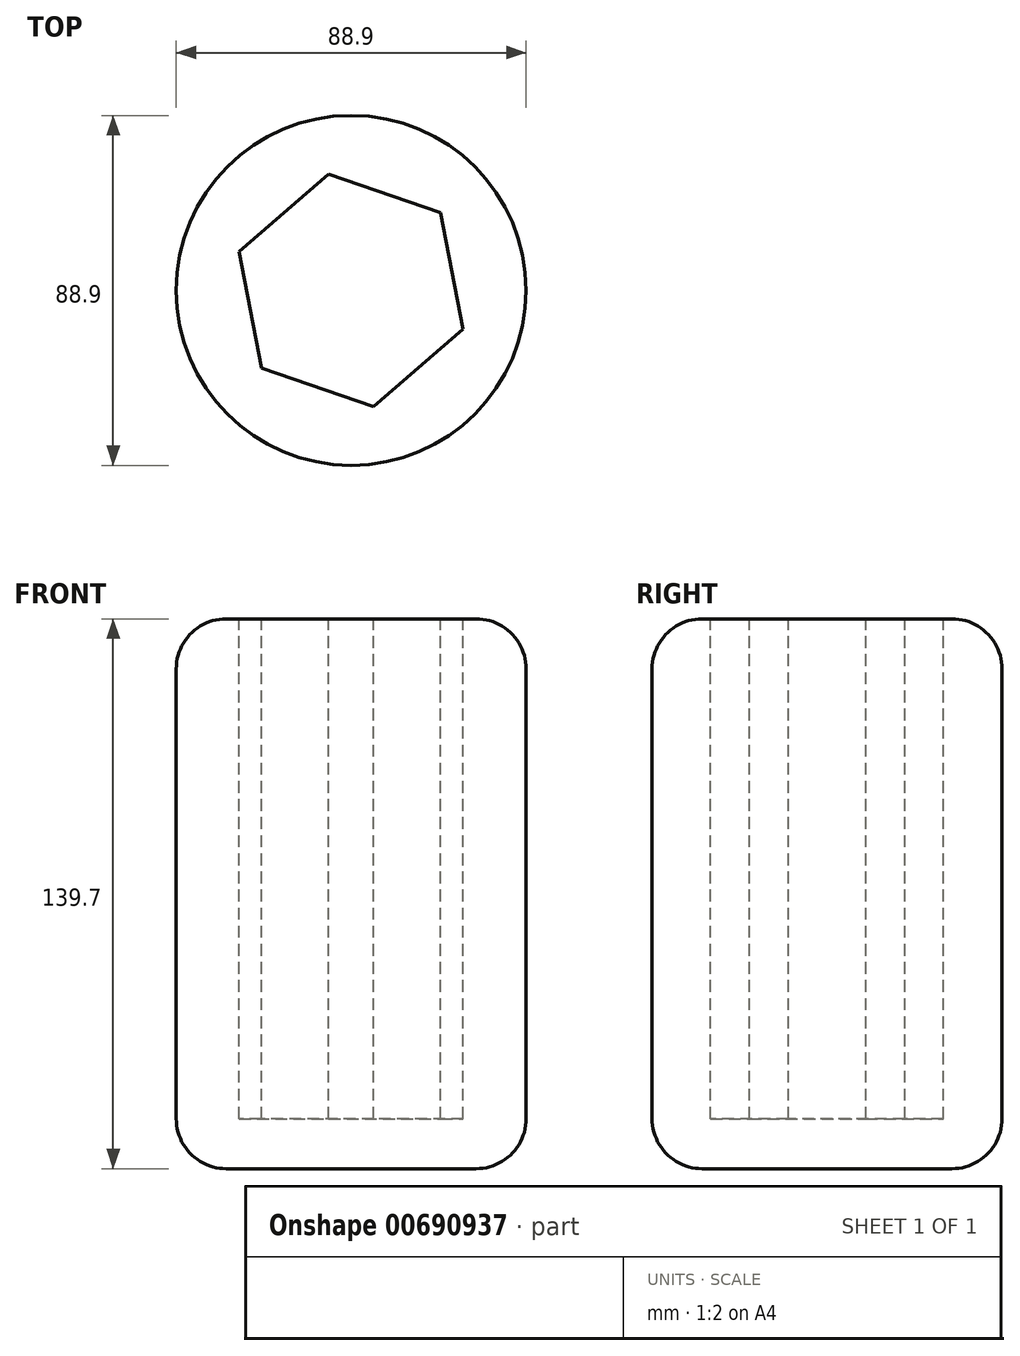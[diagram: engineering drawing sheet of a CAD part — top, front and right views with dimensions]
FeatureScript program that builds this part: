
annotation { "Feature Type Name" : "Feature", "Feature Type Description" : "" }
export const myFeature = defineFeature(function(context is Context, id is Id, definition is map)
    precondition{}
    {
        {
            var Q0;
            Q0=qCreatedBy(makeId("Top.planeOp"),FACE);
            var sketch = newSketch(context, id + "F0", { "sketchPlane" : qUnion([Q0])});
            skCircle(sketch, "E0", {"center": v(0, 0) * mm, "radius": 44.45 * mm});
            skSolve(sketch);
        }
        {
            var Q0;
            Q0 = qSketchRegion(id + "F0", true);
            extrude(context, id + "F1", {"entities" : qUnion([Q0]), "depth" : 139.7 * mm, "offsetDistance" : 25.4 * mm});
        }
        {
            var Q0;
            Q0=makeQuery(id+"F1.opExtrude","CAP_EDGE",EDGE,{"disambiguationData":[OSD([sQuery(id+"F0.wireOp",EDGE,"E0")])],"isStart":true});
            var Q1;
            Q1=makeQuery(id+"F1.opExtrude","CAP_EDGE",EDGE,{"disambiguationData":[OSD([sQuery(id+"F0.wireOp",EDGE,"E0")])],"isStart":false});
            fillet(context, id + "F2", {"entities" : qUnion([Q0, Q1]), "radius" : 12.7 * mm, "tangentPropagation" : true, "allowEdgeOverflow" : false});
        }
        {
            var Q0;
            Q0=makeQuery(id+"F1.opExtrude","CAP_FACE",FACE,{"disambiguationData":[OSD([sQuery(id+"F0.wireOp",EDGE,"E0")])],"isStart":false});
            var sketch = newSketch(context, id + "F3", { "sketchPlane" : qUnion([Q0])});
            skCircle(sketch, "E1", {"center": v(0, 0) * mm, "radius": 22.92 * mm});
            skSolve(sketch);
        }
        {
            var Q0;
            Q0 = qSketchRegion(id + "F3", true);
            extrude(context, id + "F4", {"entities" : qUnion([Q0]), "operationType" : NewBodyOperationType.REMOVE, "oppositeDirection" : true, "depth" : 127 * mm, "offsetDistance" : 25.4 * mm});
        }
        {
            var Q0;
            Q0=makeQuery(id+"F1.opExtrude","CAP_FACE",FACE,{"disambiguationData":[OSD([sQuery(id+"F0.wireOp",EDGE,"E0")])],"isStart":false});
            var sketch = newSketch(context, id + "F5", { "sketchPlane" : qUnion([Q0])});
            skCircle(sketch, "E2.cCircle", {"center": v(0, 0) * mm, "radius": 26.08 * mm, "construction": true});
            skLineSegment(sketch, "E2.0", {"start": v(22.76, 19.73) * mm, "end": v(28.46, -9.84) * mm});
            skLineSegment(sketch, "E2.1", {"start": v(28.46, -9.84) * mm, "end": v(5.7, -29.57) * mm});
            skLineSegment(sketch, "E2.2", {"start": v(5.7, -29.57) * mm, "end": v(-22.76, -19.73) * mm});
            skLineSegment(sketch, "E2.3", {"start": v(-22.76, -19.73) * mm, "end": v(-28.46, 9.84) * mm});
            skLineSegment(sketch, "E2.4", {"start": v(-28.46, 9.84) * mm, "end": v(-5.7, 29.57) * mm});
            skLineSegment(sketch, "E2.5", {"start": v(-5.7, 29.57) * mm, "end": v(22.76, 19.73) * mm});
            skPoint(sketch, "E2.0.midPoint", {"position": v(25.6, 4.94) * mm});
            skSolve(sketch);
        }
        {
            var Q0;
            Q0 = qSketchRegion(id + "F5", true);
            extrude(context, id + "F6", {"entities" : qUnion([Q0]), "operationType" : NewBodyOperationType.REMOVE, "oppositeDirection" : true, "depth" : 127 * mm, "offsetDistance" : 25.4 * mm});
        }
    });
